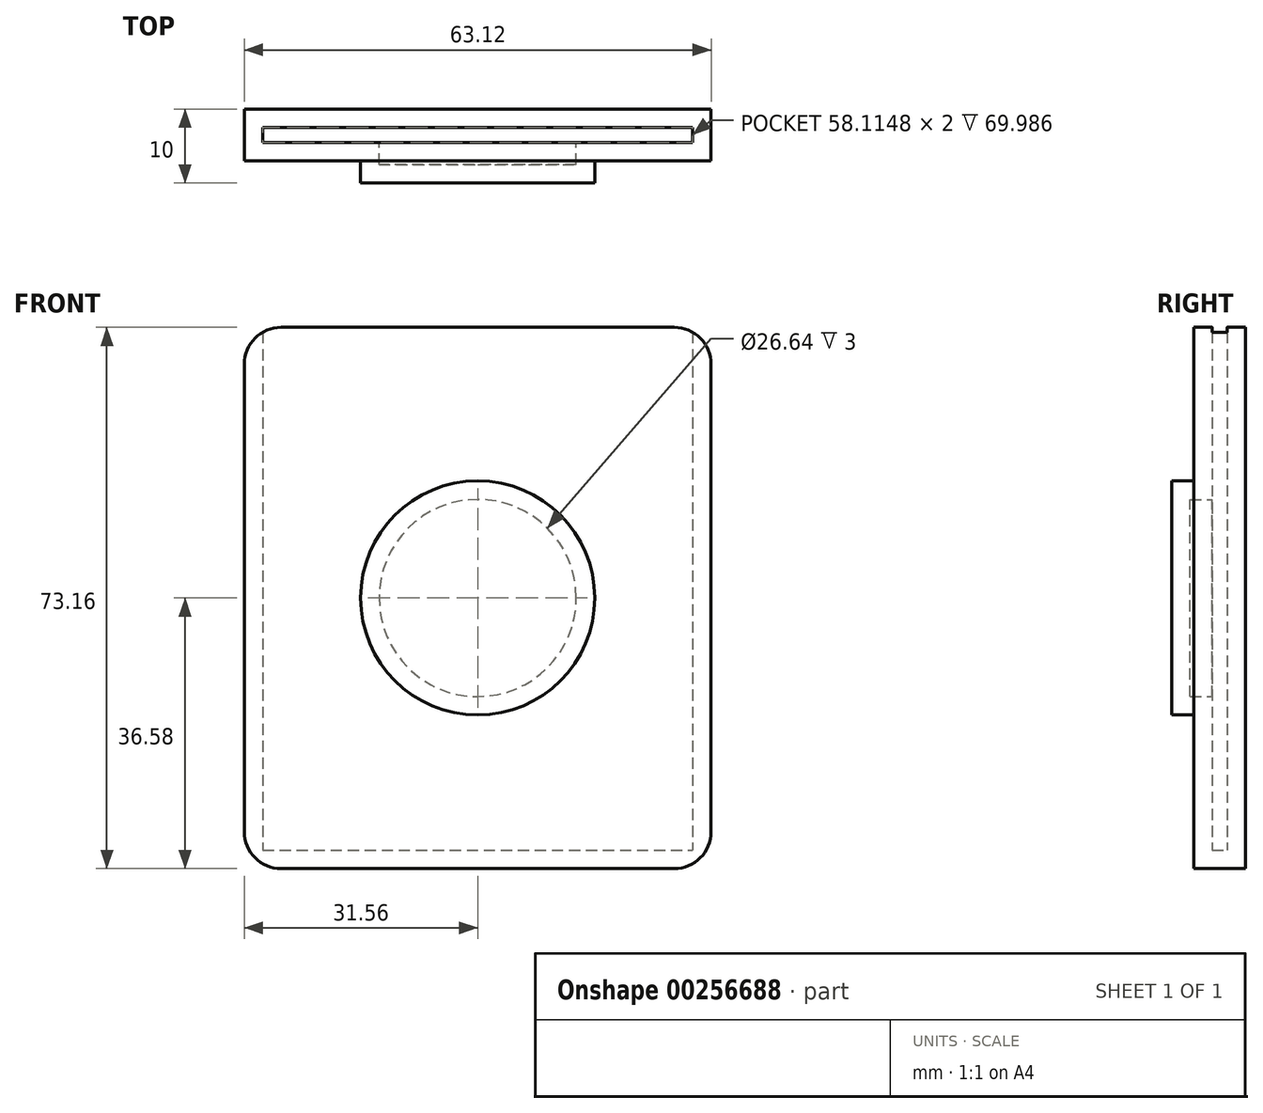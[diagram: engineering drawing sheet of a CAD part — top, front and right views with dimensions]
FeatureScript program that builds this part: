
annotation { "Feature Type Name" : "Feature", "Feature Type Description" : "" }
export const myFeature = defineFeature(function(context is Context, id is Id, definition is map)
    precondition{}
    {
        {
            var Q0;
            Q0=qCreatedBy(makeId("Front.planeOp"),FACE);
            var sketch = newSketch(context, id + "F0", { "sketchPlane" : qUnion([Q0])});
            skLineSegment(sketch, "E0.bottom", {"start": v(-31.56, 36.58) * mm, "end": v(31.56, 36.58) * mm});
            skLineSegment(sketch, "E0.top", {"start": v(-31.56, -36.58) * mm, "end": v(31.56, -36.58) * mm});
            skLineSegment(sketch, "E0.left", {"start": v(-31.56, 36.58) * mm, "end": v(-31.56, -36.58) * mm});
            skLineSegment(sketch, "E0.right", {"start": v(31.56, 36.58) * mm, "end": v(31.56, -36.58) * mm});
            skPoint(sketch, "E0.middle", {"position": v(0, 0) * mm});
            skSolve(sketch);
        }
        {
            var Q0;
            Q0=makeQuery(id+"F0.imprint","IMPRINT",FACE,{"disambiguationData":[TD([[makeQuery(id+"F0.imprint","IMPRINT",EDGE,{"derivedFrom":sQuery(id+"F0.wireOp",EDGE,"E0.bottom")}),-1.0]])]});
            extrude(context, id + "F1", {"entities" : qUnion([Q0]), "depth" : 7 * mm});
        }
        {
            var Q0;
            Q0=makeQuery(id+"F1.opExtrude","CAP_FACE",FACE,{"disambiguationData":[OSD([sQuery(id+"F0.wireOp",EDGE,"E0.bottom"),sQuery(id+"F0.wireOp",EDGE,"E0.top"),sQuery(id+"F0.wireOp",EDGE,"E0.left"),sQuery(id+"F0.wireOp",EDGE,"E0.right")])],"isStart":false});
            var sketch = newSketch(context, id + "F2", { "sketchPlane" : qUnion([Q0])});
            skCircle(sketch, "E1", {"center": v(0, 0) * mm, "radius": 15.82 * mm});
            skSolve(sketch);
        }
        {
            var Q0;
            Q0=makeQuery(id+"F2.imprint","IMPRINT",FACE,{"disambiguationData":[TD([[makeQuery(id+"F2.imprint","IMPRINT",EDGE,{"derivedFrom":sQuery(id+"F2.wireOp",EDGE,"E1")}),1.0]])]});
            extrude(context, id + "F3", {"entities" : qUnion([Q0]), "operationType" : NewBodyOperationType.ADD, "depth" : 3 * mm});
        }
        {
            var Q0;
            Q0=makeQuery(id+"F1.opExtrude","SWEPT_FACE",FACE,{"disambiguationData":[OSD([sQuery(id+"F0.wireOp",EDGE,"E0.bottom")])]});
            shell(context, id + "F4", {"entities" : qUnion([Q0]), "thickness" : 2.5 * mm});
        }
        {
            var Q0;
            Q0=makeQuery(id+"F1.opExtrude","SWEPT_EDGE",EDGE,{"disambiguationData":[OSD([sQuery(id+"F0.wireOp",EDGE,"E0.bottom"),sQuery(id+"F0.wireOp",EDGE,"E0.right")])]});
            var Q1;
            Q1=makeQuery(id+"F1.opExtrude","SWEPT_EDGE",EDGE,{"disambiguationData":[OSD([sQuery(id+"F0.wireOp",EDGE,"E0.top"),sQuery(id+"F0.wireOp",EDGE,"E0.right")])]});
            var Q2;
            Q2=makeQuery(id+"F1.opExtrude","SWEPT_EDGE",EDGE,{"disambiguationData":[OSD([sQuery(id+"F0.wireOp",EDGE,"E0.top"),sQuery(id+"F0.wireOp",EDGE,"E0.left")])]});
            var Q3;
            Q3=makeQuery(id+"F1.opExtrude","SWEPT_EDGE",EDGE,{"disambiguationData":[OSD([sQuery(id+"F0.wireOp",EDGE,"E0.bottom"),sQuery(id+"F0.wireOp",EDGE,"E0.left")])]});
            fillet(context, id + "F5", {"entities" : qUnion([Q0, Q1, Q2, Q3]), "radius" : 5 * mm, "tangentPropagation" : true, "allowEdgeOverflow" : false});
        }
    });
